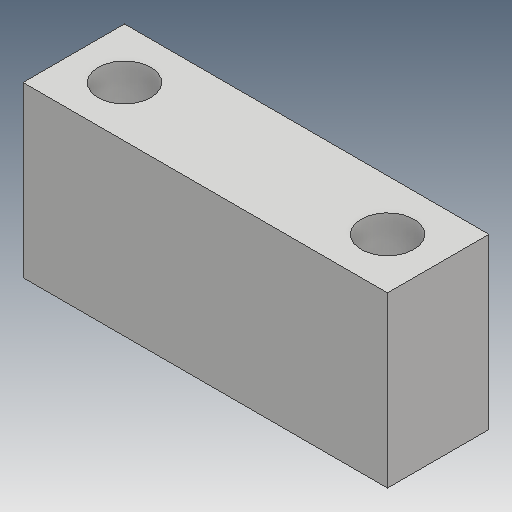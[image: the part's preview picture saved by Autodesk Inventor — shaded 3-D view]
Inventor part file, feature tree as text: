
AUTODESK INVENTOR PART (.ipt)
format: ipt  version: 2018 (Build 220112000, 112)  size: 94,208 bytes
history: native  units: mm
features: reference x6, other x4, extrude x1, sketch x1
ambient origin geometry x8: Origin, YZ Plane, XZ Plane, XY Plane, X Axis, Y Axis, Z Axis, Center Point
bodies: Volumenkörper1 (feature_tree)
feature tree (12):
  extrude  "Extrusion1"  Depth=10.0mm
  sketch  "Skizze1"  dims[d2=3.0mm d3=3.0mm d4=3.0mm d5=3.0mm d6=10.0mm d7=0.0mm]
  reference  "Referenz1"
  reference  "Referenz2"
  reference  "Referenz3"
  reference  "Referenz4"
  reference  "Referenz5"
  reference  "Referenz6"
  other  "<userpath>\OneDrive\Development\RTW\03_Konstruktion\Mohne komplett.iam"
  other  "Mohne komplett.iam"
  other  "MPU 6050 IMU:1"
  other  "Base:1"
